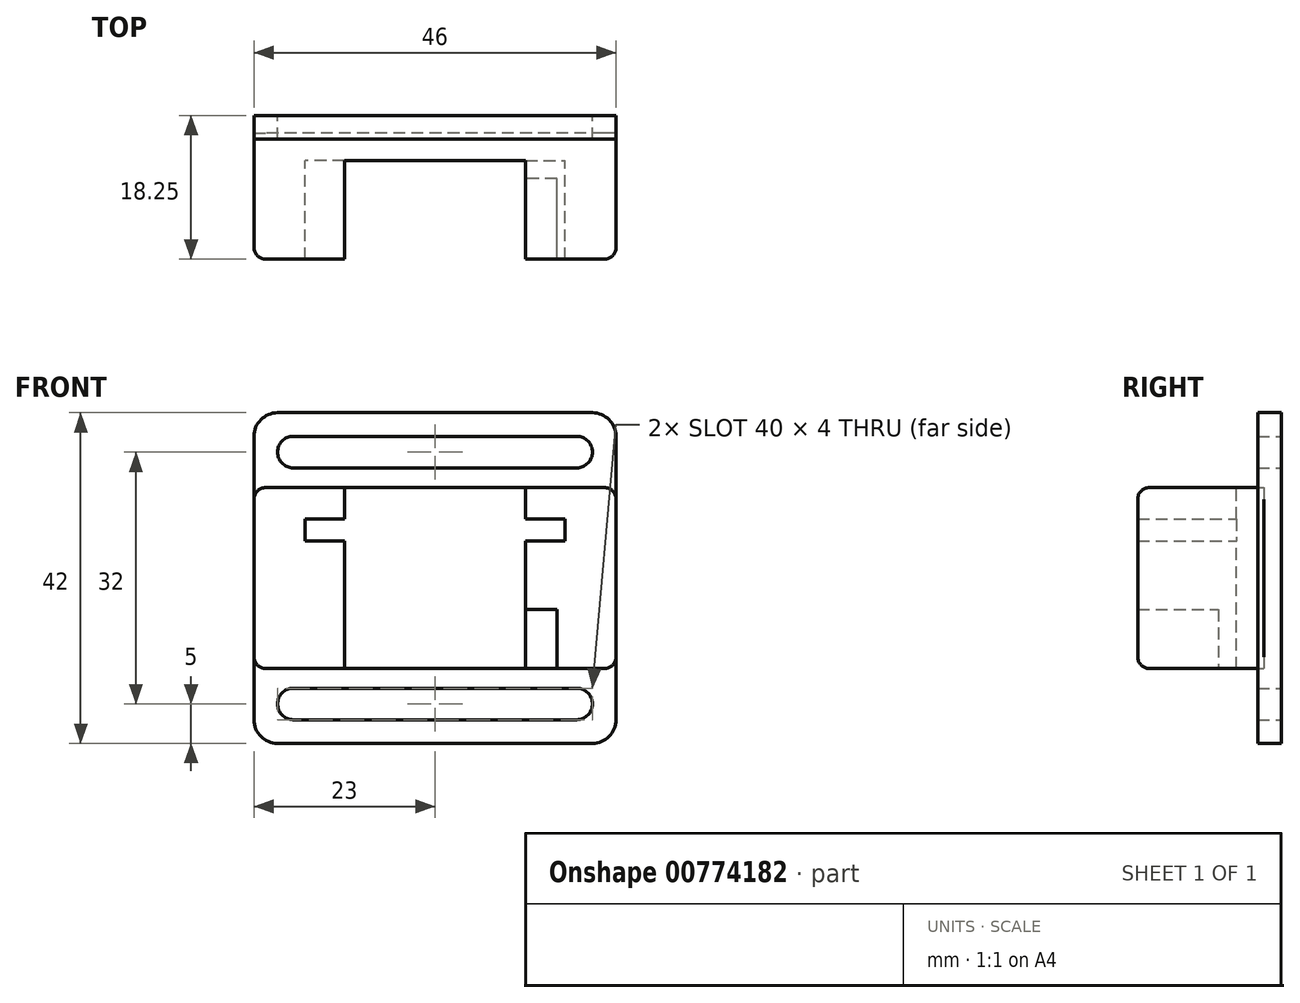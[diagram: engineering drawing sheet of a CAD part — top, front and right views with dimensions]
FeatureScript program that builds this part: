
annotation { "Feature Type Name" : "Feature", "Feature Type Description" : "" }
export const myFeature = defineFeature(function(context is Context, id is Id, definition is map)
    precondition{}
    {
        {
            var Q0;
            Q0=qCreatedBy(makeId("Front.planeOp"),FACE);
            var sketch = newSketch(context, id + "F0", { "sketchPlane" : qUnion([Q0])});
            skLineSegment(sketch, "E0.bottom", {"start": v(11.5, -11.5) * mm, "end": v(-11.5, -11.5) * mm});
            skLineSegment(sketch, "E0.top", {"start": v(11.5, 11.5) * mm, "end": v(-11.5, 11.5) * mm});
            skLineSegment(sketch, "E0.left", {"start": v(11.5, -11.5) * mm, "end": v(11.5, 11.5) * mm});
            skLineSegment(sketch, "E0.right", {"start": v(-11.5, -11.5) * mm, "end": v(-11.5, 11.5) * mm});
            skPoint(sketch, "E0.middle", {"position": v(0, 0) * mm});
            skLineSegment(sketch, "E1", {"start": v(11.5, 11.5) * mm, "end": v(11.5, 7.5) * mm});
            skLineSegment(sketch, "E2", {"start": v(11.5, 7.5) * mm, "end": v(16.5, 7.5) * mm});
            skLineSegment(sketch, "E3", {"start": v(16.5, 7.5) * mm, "end": v(16.5, 4.7) * mm});
            skLineSegment(sketch, "E4", {"start": v(16.5, 4.7) * mm, "end": v(11.5, 4.7) * mm});
            skLineSegment(sketch, "E5", {"start": v(-11.5, 11.5) * mm, "end": v(-11.5, 7.5) * mm});
            skLineSegment(sketch, "E6", {"start": v(-11.5, 7.5) * mm, "end": v(-16.5, 7.5) * mm});
            skLineSegment(sketch, "E7", {"start": v(-16.5, 7.5) * mm, "end": v(-16.5, 4.7) * mm});
            skLineSegment(sketch, "E8", {"start": v(-16.5, 4.7) * mm, "end": v(-11.5, 4.7) * mm});
            skSolve(sketch);
        }
        {
            var Q0;
            {var subQ2=sQuery(id+"F0.wireOp",EDGE,"E2");var subQ4=sQuery(id+"F0.wireOp",EDGE,"E0.bottom");var subQ11=sQuery(id+"F0.wireOp",EDGE,"E6");Q0=qUnion([makeQuery(id+"F0.imprint","IMPRINT",FACE,{"disambiguationData":[TD([[makeQuery(id+"F0.imprint","IMPRINT",EDGE,{"derivedFrom":subQ2}),-1.0]])]}),makeQuery(id+"F0.imprint","IMPRINT",FACE,{"disambiguationData":[TD([[makeQuery(id+"F0.imprint","IMPRINT",EDGE,{"derivedFrom":subQ11}),1.0]])]}),makeQuery(id+"F0.imprint","IMPRINT",FACE,{"disambiguationData":[TD([[makeQuery(id+"F0.imprint","IMPRINT",EDGE,{"derivedFrom":subQ4}),-1.0]])]})]);}
            extrude(context, id + "F1", {"entities" : qUnion([Q0]), "endBound" : BoundingType.SYMMETRIC, "depth" : 12.6 * mm, "offsetDistance" : 25 * mm});
        }
        {
            var Q0;
            Q0=qCreatedBy(makeId("Front.planeOp"),FACE);
            var sketch = newSketch(context, id + "F2", { "sketchPlane" : qUnion([Q0])});
            skLineSegment(sketch, "E9.bottom", {"start": v(23, -11.5) * mm, "end": v(-23, -11.5) * mm});
            skLineSegment(sketch, "E9.top", {"start": v(23, 11.5) * mm, "end": v(-23, 11.5) * mm});
            skLineSegment(sketch, "E9.left", {"start": v(23, -11.5) * mm, "end": v(23, 11.5) * mm});
            skLineSegment(sketch, "E9.right", {"start": v(-23, -11.5) * mm, "end": v(-23, 11.5) * mm});
            skPoint(sketch, "E9.middle", {"position": v(0, 0) * mm});
            skSolve(sketch);
        }
        {
            var Q0;
            Q0 = qSketchRegion(id + "F2", true);
            extrude(context, id + "F3", {"entities" : qUnion([Q0]), "depth" : 16 * mm, "offsetDistance" : 25 * mm});
        }
        {
            var Q0;
            Q0=makeQuery(id+"F3.opExtrude","SWEPT_BODY",BODY,{"disambiguationData":[OSD([sQuery(id+"F2.wireOp",EDGE,"E9.bottom"),sQuery(id+"F2.wireOp",EDGE,"E9.top"),sQuery(id+"F2.wireOp",EDGE,"E9.left"),sQuery(id+"F2.wireOp",EDGE,"E9.right")])]});
            transform(context, id + "F4", {"entities" : qUnion([Q0]), "transformType" : TransformType.TRANSLATION_3D, "dx" : 0 * mm, "dy" : 9.75 * mm, "dz" : 0 * mm, "makeCopy" : false});
        }
        {
            var Q0;
            Q0=qCreatedBy(makeId("Front.planeOp"),FACE);
            var sketch = newSketch(context, id + "F5", { "sketchPlane" : qUnion([Q0])});
            skLineSegment(sketch, "E10", {"start": v(0, 0) * mm, "end": v(11.5, 0) * mm});
            skLineSegment(sketch, "E11", {"start": v(11.5, 0) * mm, "end": v(11.5, -4) * mm});
            skLineSegment(sketch, "E12", {"start": v(11.5, -4) * mm, "end": v(15.5, -4) * mm});
            skLineSegment(sketch, "E13", {"start": v(15.5, -4) * mm, "end": v(15.5, -11.5) * mm});
            skLineSegment(sketch, "E14", {"start": v(15.5, -11.5) * mm, "end": v(11.5, -11.5) * mm});
            skLineSegment(sketch, "E15", {"start": v(11.5, -11.5) * mm, "end": v(11.5, -4) * mm});
            skSolve(sketch);
        }
        {
            var Q0;
            Q0 = qSketchRegion(id + "F5", true);
            extrude(context, id + "F6", {"entities" : qUnion([Q0]), "depth" : 25 * mm, "offsetDistance" : 25 * mm});
        }
        {
            var Q0;
            Q0=makeQuery(id+"F6.opExtrude","SWEPT_BODY",BODY,{"disambiguationData":[OSD([sQuery(id+"F5.wireOp",EDGE,"E12"),sQuery(id+"F5.wireOp",EDGE,"E13"),sQuery(id+"F5.wireOp",EDGE,"E14"),sQuery(id+"F5.wireOp",EDGE,"E15")])]});
            transform(context, id + "F7", {"entities" : qUnion([Q0]), "transformType" : TransformType.TRANSLATION_3D, "dx" : 0 * mm, "dy" : 4 * mm, "dz" : 0 * mm, "makeCopy" : false});
        }
        {
            var Q0;
            Q0=makeQuery(id+"F6.opExtrude","SWEPT_BODY",BODY,{"disambiguationData":[OSD([sQuery(id+"F5.wireOp",EDGE,"E12"),sQuery(id+"F5.wireOp",EDGE,"E13"),sQuery(id+"F5.wireOp",EDGE,"E14"),sQuery(id+"F5.wireOp",EDGE,"E15")])]});
            var Q1;
            Q1=makeQuery(id+"F1.opExtrude","SWEPT_BODY",BODY,{"disambiguationData":[OSD([sQuery(id+"F0.wireOp",EDGE,"E0.bottom"),sQuery(id+"F0.wireOp",EDGE,"E0.top"),sQuery(id+"F0.wireOp",EDGE,"E0.left"),sQuery(id+"F0.wireOp",EDGE,"E0.right"),sQuery(id+"F0.wireOp",EDGE,"E2"),sQuery(id+"F0.wireOp",EDGE,"E3"),sQuery(id+"F0.wireOp",EDGE,"E4"),sQuery(id+"F0.wireOp",EDGE,"E6"),sQuery(id+"F0.wireOp",EDGE,"E7"),sQuery(id+"F0.wireOp",EDGE,"E8")])]});
            var Q2;
            Q2=makeQuery(id+"F3.opExtrude","SWEPT_BODY",BODY,{"disambiguationData":[OSD([sQuery(id+"F2.wireOp",EDGE,"E9.bottom"),sQuery(id+"F2.wireOp",EDGE,"E9.top"),sQuery(id+"F2.wireOp",EDGE,"E9.left"),sQuery(id+"F2.wireOp",EDGE,"E9.right")])]});
            booleanBodies(context, id + "F8", {"operationType" : BooleanOperationType.SUBTRACTION, "tools" : qUnion([Q0, Q1]), "targets" : qUnion([Q2])});
        }
        {
            var Q0;
            Q0=makeQuery(id+"F3.opExtrude","CAP_EDGE",EDGE,{"disambiguationData":[OSD([sQuery(id+"F2.wireOp",EDGE,"E9.right")])],"isStart":false});
            var Q1;
            Q1=makeQuery(id+"F3.opExtrude","CAP_EDGE",EDGE,{"disambiguationData":[OSD([sQuery(id+"F2.wireOp",EDGE,"E9.left")])],"isStart":false});
            var Q2;
            Q2=makeQuery(id+"F3.opExtrude","SWEPT_EDGE",EDGE,{"disambiguationData":[OSD([sQuery(id+"F2.wireOp",EDGE,"E9.top"),sQuery(id+"F2.wireOp",EDGE,"E9.left")])]});
            var Q3;
            Q3=makeQuery(id+"F3.opExtrude","SWEPT_EDGE",EDGE,{"disambiguationData":[OSD([sQuery(id+"F2.wireOp",EDGE,"E9.top"),sQuery(id+"F2.wireOp",EDGE,"E9.right")])]});
            var Q4;
            {var subQ1=sQuery(id+"F2.wireOp",EDGE,"E9.right");var subQ2=sQuery(id+"F2.wireOp",EDGE,"E9.top");Q4=makeQuery(id+"F8.opBoolean","SPLIT",EDGE,{"disambiguationData":[TD([makeQuery(id+"F3.opExtrude","SWEPT_FACE",FACE,{"disambiguationData":[OSD([subQ1])]})])],"derivedFrom":makeQuery(id+"F3.opExtrude","CAP_EDGE",EDGE,{"disambiguationData":[OSD([subQ2])],"isStart":false})});}
            var Q5;
            {var subQ1=sQuery(id+"F2.wireOp",EDGE,"E9.left");var subQ2=sQuery(id+"F2.wireOp",EDGE,"E9.top");Q5=makeQuery(id+"F8.opBoolean","SPLIT",EDGE,{"disambiguationData":[TD([makeQuery(id+"F3.opExtrude","SWEPT_FACE",FACE,{"disambiguationData":[OSD([subQ1])]})])],"derivedFrom":makeQuery(id+"F3.opExtrude","CAP_EDGE",EDGE,{"disambiguationData":[OSD([subQ2])],"isStart":false})});}
            var Q6;
            Q6=makeQuery(id+"F3.opExtrude","SWEPT_EDGE",EDGE,{"disambiguationData":[OSD([sQuery(id+"F2.wireOp",EDGE,"E9.bottom"),sQuery(id+"F2.wireOp",EDGE,"E9.left")])]});
            var Q7;
            {var subQ0=sQuery(id+"F2.wireOp",EDGE,"E9.bottom");var subQ1=sQuery(id+"F2.wireOp",EDGE,"E9.left");Q7=makeQuery(id+"F8.opBoolean","SPLIT",EDGE,{"disambiguationData":[TD([makeQuery(id+"F3.opExtrude","SWEPT_FACE",FACE,{"disambiguationData":[OSD([subQ1])]})])],"derivedFrom":makeQuery(id+"F3.opExtrude","CAP_EDGE",EDGE,{"disambiguationData":[OSD([subQ0])],"isStart":false})});}
            var Q8;
            Q8=makeQuery(id+"F3.opExtrude","SWEPT_EDGE",EDGE,{"disambiguationData":[OSD([sQuery(id+"F2.wireOp",EDGE,"E9.bottom"),sQuery(id+"F2.wireOp",EDGE,"E9.right")])]});
            var Q9;
            {var subQ1=sQuery(id+"F2.wireOp",EDGE,"E9.bottom");var subQ2=sQuery(id+"F2.wireOp",EDGE,"E9.right");Q9=makeQuery(id+"F8.opBoolean","SPLIT",EDGE,{"disambiguationData":[TD([makeQuery(id+"F3.opExtrude","SWEPT_FACE",FACE,{"disambiguationData":[OSD([subQ2])]})])],"derivedFrom":makeQuery(id+"F3.opExtrude","CAP_EDGE",EDGE,{"disambiguationData":[OSD([subQ1])],"isStart":false})});}
            fillet(context, id + "F9", {"entities" : qUnion([Q0, Q1, Q2, Q3, Q4, Q5, Q6, Q7, Q8, Q9]), "radius" : 1.5 * mm, "tangentPropagation" : true, "allowEdgeOverflow" : false});
        }
        {
            var Q0;
            Q0=qCreatedBy(makeId("Front.planeOp"),FACE);
            var sketch = newSketch(context, id + "F10", { "sketchPlane" : qUnion([Q0])});
            skLineSegment(sketch, "E16.bottom", {"start": v(23, -21) * mm, "end": v(-23, -21) * mm});
            skLineSegment(sketch, "E16.top", {"start": v(23, 21) * mm, "end": v(-23, 21) * mm});
            skLineSegment(sketch, "E16.left", {"start": v(23, -21) * mm, "end": v(23, 21) * mm});
            skLineSegment(sketch, "E16.right", {"start": v(-23, -21) * mm, "end": v(-23, 21) * mm});
            skPoint(sketch, "E16.middle", {"position": v(0, 0) * mm});
            skLineSegment(sketch, "E17", {"start": v(0, 0) * mm, "end": v(0, 16) * mm});
            skLineSegment(sketch, "E18", {"start": v(0, 16) * mm, "end": v(18, 16) * mm});
            skLineSegment(sketch, "E19", {"start": v(0, 16) * mm, "end": v(-18, 16) * mm});
            skLineSegment(sketch, "E20", {"start": v(0, 0) * mm, "end": v(0, -16) * mm});
            skLineSegment(sketch, "E21", {"start": v(0, -16) * mm, "end": v(18, -16) * mm});
            skLineSegment(sketch, "E22", {"start": v(0, -16) * mm, "end": v(-18, -16) * mm});
            skLineSegment(sketch, "E23", {"start": v(-18, 16) * mm, "end": v(-18, 18) * mm});
            skLineSegment(sketch, "E24", {"start": v(18, 16) * mm, "end": v(18, 14) * mm});
            skLineSegment(sketch, "E25", {"start": v(-18, -16) * mm, "end": v(-18, -14) * mm});
            skLineSegment(sketch, "E26", {"start": v(18, -16) * mm, "end": v(18, -18) * mm});
            skArc(sketch, "E27", {"start": v(-18, 18) * mm, "mid": v(-20, 16) * mm, "end": v(-18, 14) * mm});
            skArc(sketch, "E28", {"start": v(18, 14) * mm, "mid": v(20, 16) * mm, "end": v(18, 18) * mm});
            skArc(sketch, "E29", {"start": v(-18, -14) * mm, "mid": v(-20, -16) * mm, "end": v(-18, -18) * mm});
            skArc(sketch, "E30", {"start": v(18, -18) * mm, "mid": v(20, -16) * mm, "end": v(18, -14) * mm});
            skLineSegment(sketch, "E31", {"start": v(-18, 18) * mm, "end": v(18, 18) * mm});
            skLineSegment(sketch, "E32", {"start": v(-18, 14) * mm, "end": v(18, 14) * mm});
            skLineSegment(sketch, "E33", {"start": v(-18, -14) * mm, "end": v(18, -14) * mm});
            skLineSegment(sketch, "E34", {"start": v(-18, -18) * mm, "end": v(18, -18) * mm});
            skSolve(sketch);
        }
        {
            var Q0;
            Q0 = qSketchRegion(id + "F10", true);
            extrude(context, id + "F11", {"entities" : qUnion([Q0]), "depth" : 3 * mm, "offsetDistance" : 25 * mm});
        }
        {
            var Q0;
            Q0=makeQuery(id+"F11.opExtrude","SWEPT_BODY",BODY,{"disambiguationData":[OSD([sQuery(id+"F10.wireOp",EDGE,"E16.bottom"),sQuery(id+"F10.wireOp",EDGE,"E16.top"),sQuery(id+"F10.wireOp",EDGE,"E16.left"),sQuery(id+"F10.wireOp",EDGE,"E16.right"),sQuery(id+"F10.wireOp",EDGE,"E27"),sQuery(id+"F10.wireOp",EDGE,"E28"),sQuery(id+"F10.wireOp",EDGE,"E29"),sQuery(id+"F10.wireOp",EDGE,"E30"),sQuery(id+"F10.wireOp",EDGE,"E31"),sQuery(id+"F10.wireOp",EDGE,"E32"),sQuery(id+"F10.wireOp",EDGE,"E33"),sQuery(id+"F10.wireOp",EDGE,"E34")])]});
            transform(context, id + "F12", {"entities" : qUnion([Q0]), "transformType" : TransformType.TRANSLATION_3D, "dx" : 0 * mm, "dy" : 12 * mm, "dz" : 0 * mm, "makeCopy" : false});
        }
        {
            var Q0;
            Q0=makeQuery(id+"F11.opExtrude","SWEPT_EDGE",EDGE,{"disambiguationData":[OSD([sQuery(id+"F10.wireOp",EDGE,"E16.top"),sQuery(id+"F10.wireOp",EDGE,"E16.right")])]});
            var Q1;
            Q1=makeQuery(id+"F11.opExtrude","SWEPT_EDGE",EDGE,{"disambiguationData":[OSD([sQuery(id+"F10.wireOp",EDGE,"E16.top"),sQuery(id+"F10.wireOp",EDGE,"E16.left")])]});
            var Q2;
            Q2=makeQuery(id+"F11.opExtrude","SWEPT_EDGE",EDGE,{"disambiguationData":[OSD([sQuery(id+"F10.wireOp",EDGE,"E16.bottom"),sQuery(id+"F10.wireOp",EDGE,"E16.left")])]});
            var Q3;
            Q3=makeQuery(id+"F11.opExtrude","SWEPT_EDGE",EDGE,{"disambiguationData":[OSD([sQuery(id+"F10.wireOp",EDGE,"E16.bottom"),sQuery(id+"F10.wireOp",EDGE,"E16.right")])]});
            fillet(context, id + "F13", {"entities" : qUnion([Q0, Q1, Q2, Q3]), "radius" : 3 * mm, "tangentPropagation" : true, "allowEdgeOverflow" : false});
        }
    });
